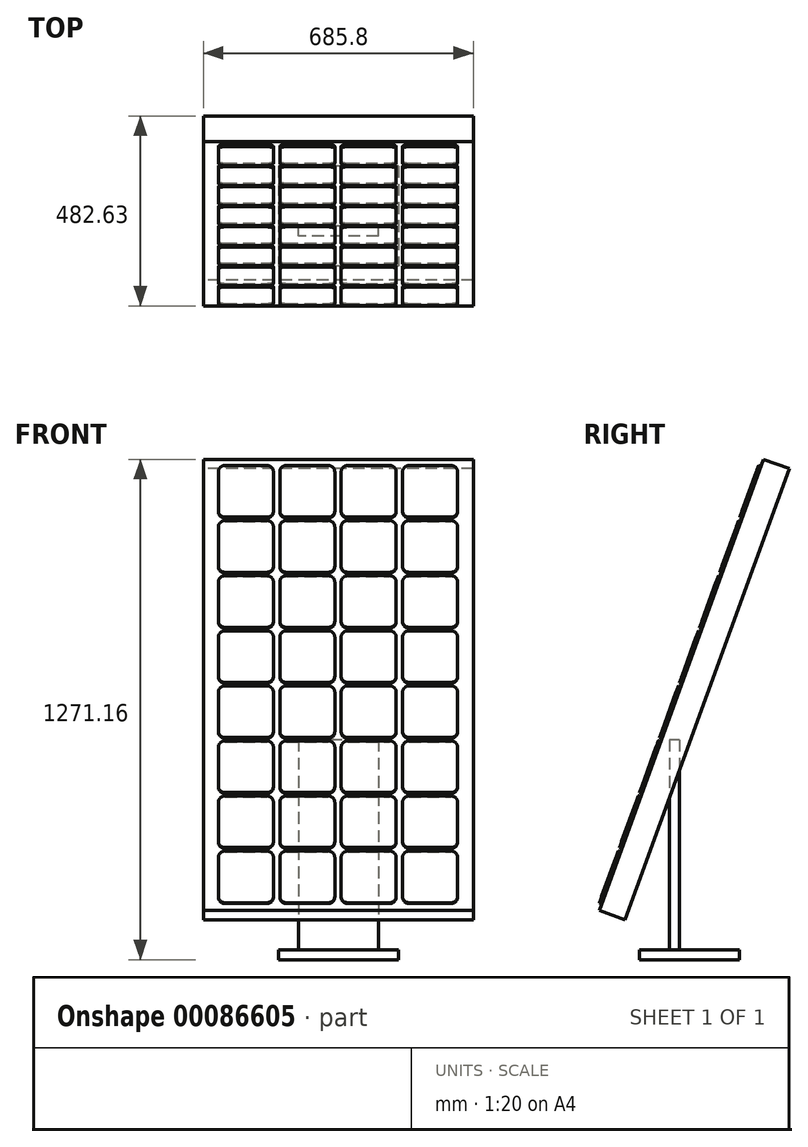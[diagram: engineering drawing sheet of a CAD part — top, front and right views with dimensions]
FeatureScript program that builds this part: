
annotation { "Feature Type Name" : "Feature", "Feature Type Description" : "" }
export const myFeature = defineFeature(function(context is Context, id is Id, definition is map)
    precondition{}
    {
        {
            var Q0;
            Q0=qCreatedBy(makeId("Right.planeOp"),FACE);
            var sketch = newSketch(context, id + "F0", { "sketchPlane" : qUnion([Q0])});
            skLineSegment(sketch, "E0", {"start": v(0, 125.5) * mm, "end": v(417, 1271.16) * mm});
            skLineSegment(sketch, "E1", {"start": v(417, 1271.16) * mm, "end": v(482.63, 1247.27) * mm});
            skLineSegment(sketch, "E2", {"start": v(482.63, 1247.27) * mm, "end": v(65.64, 101.6) * mm});
            skLineSegment(sketch, "E3", {"start": v(65.64, 101.6) * mm, "end": v(0, 125.5) * mm});
            skLineSegment(sketch, "E4", {"start": v(0, 0) * mm, "end": v(325.35, 0) * mm, "construction": true});
            skSolve(sketch);
        }
        {
            var Q0;
            Q0 = qSketchRegion(id + "F0", true);
            extrude(context, id + "F1", {"entities" : qUnion([Q0]), "depth" : 342.9 * mm, "hasSecondDirection" : true, "secondDirectionOppositeDirection" : true, "secondDirectionDepth" : 342.9 * mm});
        }
        {
            var Q0;
            Q0=qCreatedBy(makeId("Right.planeOp"),FACE);
            var sketch = newSketch(context, id + "F2", { "sketchPlane" : qUnion([Q0])});
            skLineSegment(sketch, "E5.bottom", {"start": v(203.2, 558.8) * mm, "end": v(177.8, 558.8) * mm});
            skLineSegment(sketch, "E5.top", {"start": v(203.2, 0) * mm, "end": v(177.8, 0) * mm});
            skLineSegment(sketch, "E5.left", {"start": v(203.2, 558.8) * mm, "end": v(203.2, 0) * mm});
            skLineSegment(sketch, "E5.right", {"start": v(177.8, 558.8) * mm, "end": v(177.8, 0) * mm});
            skSolve(sketch);
        }
        {
            var Q0;
            Q0 = qSketchRegion(id + "F2", true);
            extrude(context, id + "F3", {"entities" : qUnion([Q0]), "depth" : 101.6 * mm, "hasSecondDirection" : true, "secondDirectionOppositeDirection" : true, "secondDirectionDepth" : 101.6 * mm});
        }
        {
            var Q0;
            Q0=makeQuery(id+"F3.opExtrude","SWEPT_FACE",FACE,{"disambiguationData":[OSD([sQuery(id+"F2.wireOp",EDGE,"E5.top")])]});
            var sketch = newSketch(context, id + "F4", { "sketchPlane" : qUnion([Q0])});
            skLineSegment(sketch, "E6.bottom", {"start": v(152.4, -355.6) * mm, "end": v(-152.4, -355.6) * mm});
            skLineSegment(sketch, "E6.top", {"start": v(152.4, -101.6) * mm, "end": v(-152.4, -101.6) * mm});
            skLineSegment(sketch, "E6.left", {"start": v(152.4, -355.6) * mm, "end": v(152.4, -101.6) * mm});
            skLineSegment(sketch, "E6.right", {"start": v(-152.4, -355.6) * mm, "end": v(-152.4, -101.6) * mm});
            skSolve(sketch);
        }
        {
            var Q0;
            Q0 = qSketchRegion(id + "F4", true);
            extrude(context, id + "F5", {"entities" : qUnion([Q0]), "operationType" : NewBodyOperationType.ADD, "oppositeDirection" : true, "depth" : 25.4 * mm});
        }
        {
            var Q0;
            Q0=makeQuery(id+"F1.opExtrude","SWEPT_FACE",FACE,{"disambiguationData":[OSD([sQuery(id+"F0.wireOp",EDGE,"E0")])]});
            var sketch = newSketch(context, id + "F6", { "sketchPlane" : qUnion([Q0])});
            skLineSegment(sketch, "E7.bottom", {"start": v(-288.04, 1318.07) * mm, "end": v(-181.86, 1318.07) * mm});
            skLineSegment(sketch, "E7.top", {"start": v(-288.04, 1178.37) * mm, "end": v(-181.86, 1178.37) * mm});
            skLineSegment(sketch, "E7.left", {"start": v(-304.8, 1301.3) * mm, "end": v(-304.8, 1195.14) * mm});
            skLineSegment(sketch, "E7.right", {"start": v(-165.1, 1301.3) * mm, "end": v(-165.1, 1195.14) * mm});
            skPoint(sketch, "E8.visualSharp", {"position": v(-304.8, 1318.07) * mm});
            skArc(sketch, "E8.filletArc", {"start": v(-288.04, 1318.07) * mm, "mid": v(-299.89, 1313.16) * mm, "end": v(-304.8, 1301.3) * mm});
            skPoint(sketch, "E9.visualSharp", {"position": v(-165.1, 1318.07) * mm});
            skArc(sketch, "E9.filletArc", {"start": v(-165.1, 1301.3) * mm, "mid": v(-170.01, 1313.16) * mm, "end": v(-181.86, 1318.07) * mm});
            skPoint(sketch, "E10.visualSharp", {"position": v(-165.1, 1178.37) * mm});
            skArc(sketch, "E10.filletArc", {"start": v(-181.86, 1178.37) * mm, "mid": v(-170.01, 1183.28) * mm, "end": v(-165.1, 1195.14) * mm});
            skPoint(sketch, "E11.visualSharp", {"position": v(-304.8, 1178.37) * mm});
            skArc(sketch, "E11.filletArc", {"start": v(-304.8, 1195.14) * mm, "mid": v(-299.89, 1183.28) * mm, "end": v(-288.04, 1178.37) * mm});
            skLineSegment(sketch, "E12.0.1.0", {"start": v(-288.04, 1169.16) * mm, "end": v(-181.86, 1169.16) * mm});
            skLineSegment(sketch, "E12.0.1.1", {"start": v(-288.04, 1029.46) * mm, "end": v(-181.86, 1029.46) * mm});
            skLineSegment(sketch, "E12.0.1.2", {"start": v(-304.8, 1152.4) * mm, "end": v(-304.8, 1046.22) * mm});
            skLineSegment(sketch, "E12.0.1.3", {"start": v(-165.1, 1152.4) * mm, "end": v(-165.1, 1046.22) * mm});
            skPoint(sketch, "E12.0.1.4", {"position": v(-304.8, 1169.16) * mm});
            skPoint(sketch, "E12.0.1.5", {"position": v(-165.1, 1169.16) * mm});
            skPoint(sketch, "E12.0.1.6", {"position": v(-165.1, 1029.46) * mm});
            skPoint(sketch, "E12.0.1.7", {"position": v(-304.8, 1029.46) * mm});
            skArc(sketch, "E12.0.1.8", {"start": v(-288.04, 1169.16) * mm, "mid": v(-299.89, 1164.25) * mm, "end": v(-304.8, 1152.4) * mm});
            skArc(sketch, "E12.0.1.9", {"start": v(-165.1, 1152.4) * mm, "mid": v(-170.01, 1164.25) * mm, "end": v(-181.86, 1169.16) * mm});
            skArc(sketch, "E12.0.1.10", {"start": v(-181.86, 1029.46) * mm, "mid": v(-170.01, 1034.37) * mm, "end": v(-165.1, 1046.22) * mm});
            skArc(sketch, "E12.0.1.11", {"start": v(-304.8, 1046.22) * mm, "mid": v(-299.89, 1034.37) * mm, "end": v(-288.04, 1029.46) * mm});
            skLineSegment(sketch, "E12.0.2.0", {"start": v(-288.04, 1020.25) * mm, "end": v(-181.86, 1020.25) * mm});
            skLineSegment(sketch, "E12.0.2.1", {"start": v(-288.04, 880.55) * mm, "end": v(-181.86, 880.55) * mm});
            skLineSegment(sketch, "E12.0.2.2", {"start": v(-304.8, 1003.48) * mm, "end": v(-304.8, 897.31) * mm});
            skLineSegment(sketch, "E12.0.2.3", {"start": v(-165.1, 1003.48) * mm, "end": v(-165.1, 897.31) * mm});
            skPoint(sketch, "E12.0.2.4", {"position": v(-304.8, 1020.25) * mm});
            skPoint(sketch, "E12.0.2.5", {"position": v(-165.1, 1020.25) * mm});
            skPoint(sketch, "E12.0.2.6", {"position": v(-165.1, 880.55) * mm});
            skPoint(sketch, "E12.0.2.7", {"position": v(-304.8, 880.55) * mm});
            skArc(sketch, "E12.0.2.8", {"start": v(-288.04, 1020.25) * mm, "mid": v(-299.89, 1015.34) * mm, "end": v(-304.8, 1003.48) * mm});
            skArc(sketch, "E12.0.2.9", {"start": v(-165.1, 1003.48) * mm, "mid": v(-170.01, 1015.34) * mm, "end": v(-181.86, 1020.25) * mm});
            skArc(sketch, "E12.0.2.10", {"start": v(-181.86, 880.55) * mm, "mid": v(-170.01, 885.46) * mm, "end": v(-165.1, 897.31) * mm});
            skArc(sketch, "E12.0.2.11", {"start": v(-304.8, 897.31) * mm, "mid": v(-299.89, 885.46) * mm, "end": v(-288.04, 880.55) * mm});
            skLineSegment(sketch, "E12.0.3.0", {"start": v(-288.04, 871.33) * mm, "end": v(-181.86, 871.33) * mm});
            skLineSegment(sketch, "E12.0.3.1", {"start": v(-288.04, 731.63) * mm, "end": v(-181.86, 731.63) * mm});
            skLineSegment(sketch, "E12.0.3.2", {"start": v(-304.8, 854.57) * mm, "end": v(-304.8, 748.4) * mm});
            skLineSegment(sketch, "E12.0.3.3", {"start": v(-165.1, 854.57) * mm, "end": v(-165.1, 748.4) * mm});
            skPoint(sketch, "E12.0.3.4", {"position": v(-304.8, 871.33) * mm});
            skPoint(sketch, "E12.0.3.5", {"position": v(-165.1, 871.33) * mm});
            skPoint(sketch, "E12.0.3.6", {"position": v(-165.1, 731.63) * mm});
            skPoint(sketch, "E12.0.3.7", {"position": v(-304.8, 731.63) * mm});
            skArc(sketch, "E12.0.3.8", {"start": v(-288.04, 871.33) * mm, "mid": v(-299.89, 866.42) * mm, "end": v(-304.8, 854.57) * mm});
            skArc(sketch, "E12.0.3.9", {"start": v(-165.1, 854.57) * mm, "mid": v(-170.01, 866.42) * mm, "end": v(-181.86, 871.33) * mm});
            skArc(sketch, "E12.0.3.10", {"start": v(-181.86, 731.63) * mm, "mid": v(-170.01, 736.54) * mm, "end": v(-165.1, 748.4) * mm});
            skArc(sketch, "E12.0.3.11", {"start": v(-304.8, 748.4) * mm, "mid": v(-299.89, 736.54) * mm, "end": v(-288.04, 731.63) * mm});
            skLineSegment(sketch, "E12.0.4.0", {"start": v(-288.04, 722.42) * mm, "end": v(-181.86, 722.42) * mm});
            skLineSegment(sketch, "E12.0.4.1", {"start": v(-288.04, 582.72) * mm, "end": v(-181.86, 582.72) * mm});
            skLineSegment(sketch, "E12.0.4.2", {"start": v(-304.8, 705.66) * mm, "end": v(-304.8, 599.49) * mm});
            skLineSegment(sketch, "E12.0.4.3", {"start": v(-165.1, 705.66) * mm, "end": v(-165.1, 599.49) * mm});
            skPoint(sketch, "E12.0.4.4", {"position": v(-304.8, 722.42) * mm});
            skPoint(sketch, "E12.0.4.5", {"position": v(-165.1, 722.42) * mm});
            skPoint(sketch, "E12.0.4.6", {"position": v(-165.1, 582.72) * mm});
            skPoint(sketch, "E12.0.4.7", {"position": v(-304.8, 582.72) * mm});
            skArc(sketch, "E12.0.4.8", {"start": v(-288.04, 722.42) * mm, "mid": v(-299.89, 717.51) * mm, "end": v(-304.8, 705.66) * mm});
            skArc(sketch, "E12.0.4.9", {"start": v(-165.1, 705.66) * mm, "mid": v(-170.01, 717.51) * mm, "end": v(-181.86, 722.42) * mm});
            skArc(sketch, "E12.0.4.10", {"start": v(-181.86, 582.72) * mm, "mid": v(-170.01, 587.63) * mm, "end": v(-165.1, 599.49) * mm});
            skArc(sketch, "E12.0.4.11", {"start": v(-304.8, 599.49) * mm, "mid": v(-299.89, 587.63) * mm, "end": v(-288.04, 582.72) * mm});
            skLineSegment(sketch, "E12.0.5.0", {"start": v(-288.04, 573.5) * mm, "end": v(-181.86, 573.5) * mm});
            skLineSegment(sketch, "E12.0.5.1", {"start": v(-288.04, 433.8) * mm, "end": v(-181.86, 433.8) * mm});
            skLineSegment(sketch, "E12.0.5.2", {"start": v(-304.8, 556.74) * mm, "end": v(-304.8, 450.57) * mm});
            skLineSegment(sketch, "E12.0.5.3", {"start": v(-165.1, 556.74) * mm, "end": v(-165.1, 450.57) * mm});
            skPoint(sketch, "E12.0.5.4", {"position": v(-304.8, 573.5) * mm});
            skPoint(sketch, "E12.0.5.5", {"position": v(-165.1, 573.5) * mm});
            skPoint(sketch, "E12.0.5.6", {"position": v(-165.1, 433.8) * mm});
            skPoint(sketch, "E12.0.5.7", {"position": v(-304.8, 433.8) * mm});
            skArc(sketch, "E12.0.5.8", {"start": v(-288.04, 573.5) * mm, "mid": v(-299.89, 568.6) * mm, "end": v(-304.8, 556.74) * mm});
            skArc(sketch, "E12.0.5.9", {"start": v(-165.1, 556.74) * mm, "mid": v(-170.01, 568.6) * mm, "end": v(-181.86, 573.5) * mm});
            skArc(sketch, "E12.0.5.10", {"start": v(-181.86, 433.8) * mm, "mid": v(-170.01, 438.72) * mm, "end": v(-165.1, 450.57) * mm});
            skArc(sketch, "E12.0.5.11", {"start": v(-304.8, 450.57) * mm, "mid": v(-299.89, 438.72) * mm, "end": v(-288.04, 433.8) * mm});
            skLineSegment(sketch, "E12.0.6.0", {"start": v(-288.04, 424.6) * mm, "end": v(-181.86, 424.6) * mm});
            skLineSegment(sketch, "E12.0.6.1", {"start": v(-288.04, 284.9) * mm, "end": v(-181.86, 284.9) * mm});
            skLineSegment(sketch, "E12.0.6.2", {"start": v(-304.8, 407.83) * mm, "end": v(-304.8, 301.66) * mm});
            skLineSegment(sketch, "E12.0.6.3", {"start": v(-165.1, 407.83) * mm, "end": v(-165.1, 301.66) * mm});
            skPoint(sketch, "E12.0.6.4", {"position": v(-304.8, 424.6) * mm});
            skPoint(sketch, "E12.0.6.5", {"position": v(-165.1, 424.6) * mm});
            skPoint(sketch, "E12.0.6.6", {"position": v(-165.1, 284.9) * mm});
            skPoint(sketch, "E12.0.6.7", {"position": v(-304.8, 284.9) * mm});
            skArc(sketch, "E12.0.6.8", {"start": v(-288.04, 424.6) * mm, "mid": v(-299.89, 419.69) * mm, "end": v(-304.8, 407.83) * mm});
            skArc(sketch, "E12.0.6.9", {"start": v(-165.1, 407.83) * mm, "mid": v(-170.01, 419.69) * mm, "end": v(-181.86, 424.6) * mm});
            skArc(sketch, "E12.0.6.10", {"start": v(-181.86, 284.9) * mm, "mid": v(-170.01, 289.8) * mm, "end": v(-165.1, 301.66) * mm});
            skArc(sketch, "E12.0.6.11", {"start": v(-304.8, 301.66) * mm, "mid": v(-299.89, 289.8) * mm, "end": v(-288.04, 284.9) * mm});
            skLineSegment(sketch, "E12.0.7.0", {"start": v(-288.04, 275.68) * mm, "end": v(-181.86, 275.68) * mm});
            skLineSegment(sketch, "E12.0.7.1", {"start": v(-288.04, 135.98) * mm, "end": v(-181.86, 135.98) * mm});
            skLineSegment(sketch, "E12.0.7.2", {"start": v(-304.8, 258.92) * mm, "end": v(-304.8, 152.75) * mm});
            skLineSegment(sketch, "E12.0.7.3", {"start": v(-165.1, 258.92) * mm, "end": v(-165.1, 152.75) * mm});
            skPoint(sketch, "E12.0.7.4", {"position": v(-304.8, 275.68) * mm});
            skPoint(sketch, "E12.0.7.5", {"position": v(-165.1, 275.68) * mm});
            skPoint(sketch, "E12.0.7.6", {"position": v(-165.1, 135.98) * mm});
            skPoint(sketch, "E12.0.7.7", {"position": v(-304.8, 135.98) * mm});
            skArc(sketch, "E12.0.7.8", {"start": v(-288.04, 275.68) * mm, "mid": v(-299.89, 270.77) * mm, "end": v(-304.8, 258.92) * mm});
            skArc(sketch, "E12.0.7.9", {"start": v(-165.1, 258.92) * mm, "mid": v(-170.01, 270.77) * mm, "end": v(-181.86, 275.68) * mm});
            skArc(sketch, "E12.0.7.10", {"start": v(-181.86, 135.98) * mm, "mid": v(-170.01, 140.9) * mm, "end": v(-165.1, 152.75) * mm});
            skArc(sketch, "E12.0.7.11", {"start": v(-304.8, 152.75) * mm, "mid": v(-299.89, 140.9) * mm, "end": v(-288.04, 135.98) * mm});
            skLineSegment(sketch, "E12.1.0.0", {"start": v(-132.07, 1318.07) * mm, "end": v(-25.9, 1318.07) * mm});
            skLineSegment(sketch, "E12.1.0.1", {"start": v(-132.07, 1178.37) * mm, "end": v(-25.9, 1178.37) * mm});
            skLineSegment(sketch, "E12.1.0.2", {"start": v(-148.84, 1301.3) * mm, "end": v(-148.84, 1195.14) * mm});
            skLineSegment(sketch, "E12.1.0.3", {"start": v(-9.14, 1301.3) * mm, "end": v(-9.14, 1195.14) * mm});
            skPoint(sketch, "E12.1.0.4", {"position": v(-148.84, 1318.07) * mm});
            skPoint(sketch, "E12.1.0.5", {"position": v(-9.14, 1318.07) * mm});
            skPoint(sketch, "E12.1.0.6", {"position": v(-9.14, 1178.37) * mm});
            skPoint(sketch, "E12.1.0.7", {"position": v(-148.84, 1178.37) * mm});
            skArc(sketch, "E12.1.0.8", {"start": v(-132.07, 1318.07) * mm, "mid": v(-143.93, 1313.16) * mm, "end": v(-148.84, 1301.3) * mm});
            skArc(sketch, "E12.1.0.9", {"start": v(-9.14, 1301.3) * mm, "mid": v(-14.05, 1313.16) * mm, "end": v(-25.9, 1318.07) * mm});
            skArc(sketch, "E12.1.0.10", {"start": v(-25.9, 1178.37) * mm, "mid": v(-14.05, 1183.28) * mm, "end": v(-9.14, 1195.14) * mm});
            skArc(sketch, "E12.1.0.11", {"start": v(-148.84, 1195.14) * mm, "mid": v(-143.93, 1183.28) * mm, "end": v(-132.07, 1178.37) * mm});
            skLineSegment(sketch, "E12.1.1.0", {"start": v(-132.07, 1169.16) * mm, "end": v(-25.9, 1169.16) * mm});
            skLineSegment(sketch, "E12.1.1.1", {"start": v(-132.07, 1029.46) * mm, "end": v(-25.9, 1029.46) * mm});
            skLineSegment(sketch, "E12.1.1.2", {"start": v(-148.84, 1152.4) * mm, "end": v(-148.84, 1046.22) * mm});
            skLineSegment(sketch, "E12.1.1.3", {"start": v(-9.14, 1152.4) * mm, "end": v(-9.14, 1046.22) * mm});
            skPoint(sketch, "E12.1.1.4", {"position": v(-148.84, 1169.16) * mm});
            skPoint(sketch, "E12.1.1.5", {"position": v(-9.14, 1169.16) * mm});
            skPoint(sketch, "E12.1.1.6", {"position": v(-9.14, 1029.46) * mm});
            skPoint(sketch, "E12.1.1.7", {"position": v(-148.84, 1029.46) * mm});
            skArc(sketch, "E12.1.1.8", {"start": v(-132.07, 1169.16) * mm, "mid": v(-143.93, 1164.25) * mm, "end": v(-148.84, 1152.4) * mm});
            skArc(sketch, "E12.1.1.9", {"start": v(-9.14, 1152.4) * mm, "mid": v(-14.05, 1164.25) * mm, "end": v(-25.9, 1169.16) * mm});
            skArc(sketch, "E12.1.1.10", {"start": v(-25.9, 1029.46) * mm, "mid": v(-14.05, 1034.37) * mm, "end": v(-9.14, 1046.22) * mm});
            skArc(sketch, "E12.1.1.11", {"start": v(-148.84, 1046.22) * mm, "mid": v(-143.93, 1034.37) * mm, "end": v(-132.07, 1029.46) * mm});
            skLineSegment(sketch, "E12.1.2.0", {"start": v(-132.07, 1020.25) * mm, "end": v(-25.9, 1020.25) * mm});
            skLineSegment(sketch, "E12.1.2.1", {"start": v(-132.07, 880.55) * mm, "end": v(-25.9, 880.55) * mm});
            skLineSegment(sketch, "E12.1.2.2", {"start": v(-148.84, 1003.48) * mm, "end": v(-148.84, 897.31) * mm});
            skLineSegment(sketch, "E12.1.2.3", {"start": v(-9.14, 1003.48) * mm, "end": v(-9.14, 897.31) * mm});
            skPoint(sketch, "E12.1.2.4", {"position": v(-148.84, 1020.25) * mm});
            skPoint(sketch, "E12.1.2.5", {"position": v(-9.14, 1020.25) * mm});
            skPoint(sketch, "E12.1.2.6", {"position": v(-9.14, 880.55) * mm});
            skPoint(sketch, "E12.1.2.7", {"position": v(-148.84, 880.55) * mm});
            skArc(sketch, "E12.1.2.8", {"start": v(-132.07, 1020.25) * mm, "mid": v(-143.93, 1015.34) * mm, "end": v(-148.84, 1003.48) * mm});
            skArc(sketch, "E12.1.2.9", {"start": v(-9.14, 1003.48) * mm, "mid": v(-14.05, 1015.34) * mm, "end": v(-25.9, 1020.25) * mm});
            skArc(sketch, "E12.1.2.10", {"start": v(-25.9, 880.55) * mm, "mid": v(-14.05, 885.46) * mm, "end": v(-9.14, 897.31) * mm});
            skArc(sketch, "E12.1.2.11", {"start": v(-148.84, 897.31) * mm, "mid": v(-143.93, 885.46) * mm, "end": v(-132.07, 880.55) * mm});
            skLineSegment(sketch, "E12.1.3.0", {"start": v(-132.07, 871.33) * mm, "end": v(-25.9, 871.33) * mm});
            skLineSegment(sketch, "E12.1.3.1", {"start": v(-132.07, 731.63) * mm, "end": v(-25.9, 731.63) * mm});
            skLineSegment(sketch, "E12.1.3.2", {"start": v(-148.84, 854.57) * mm, "end": v(-148.84, 748.4) * mm});
            skLineSegment(sketch, "E12.1.3.3", {"start": v(-9.14, 854.57) * mm, "end": v(-9.14, 748.4) * mm});
            skPoint(sketch, "E12.1.3.4", {"position": v(-148.84, 871.33) * mm});
            skPoint(sketch, "E12.1.3.5", {"position": v(-9.14, 871.33) * mm});
            skPoint(sketch, "E12.1.3.6", {"position": v(-9.14, 731.63) * mm});
            skPoint(sketch, "E12.1.3.7", {"position": v(-148.84, 731.63) * mm});
            skArc(sketch, "E12.1.3.8", {"start": v(-132.07, 871.33) * mm, "mid": v(-143.93, 866.42) * mm, "end": v(-148.84, 854.57) * mm});
            skArc(sketch, "E12.1.3.9", {"start": v(-9.14, 854.57) * mm, "mid": v(-14.05, 866.42) * mm, "end": v(-25.9, 871.33) * mm});
            skArc(sketch, "E12.1.3.10", {"start": v(-25.9, 731.63) * mm, "mid": v(-14.05, 736.54) * mm, "end": v(-9.14, 748.4) * mm});
            skArc(sketch, "E12.1.3.11", {"start": v(-148.84, 748.4) * mm, "mid": v(-143.93, 736.54) * mm, "end": v(-132.07, 731.63) * mm});
            skLineSegment(sketch, "E12.1.4.0", {"start": v(-132.07, 722.42) * mm, "end": v(-25.9, 722.42) * mm});
            skLineSegment(sketch, "E12.1.4.1", {"start": v(-132.07, 582.72) * mm, "end": v(-25.9, 582.72) * mm});
            skLineSegment(sketch, "E12.1.4.2", {"start": v(-148.84, 705.66) * mm, "end": v(-148.84, 599.49) * mm});
            skLineSegment(sketch, "E12.1.4.3", {"start": v(-9.14, 705.66) * mm, "end": v(-9.14, 599.49) * mm});
            skPoint(sketch, "E12.1.4.4", {"position": v(-148.84, 722.42) * mm});
            skPoint(sketch, "E12.1.4.5", {"position": v(-9.14, 722.42) * mm});
            skPoint(sketch, "E12.1.4.6", {"position": v(-9.14, 582.72) * mm});
            skPoint(sketch, "E12.1.4.7", {"position": v(-148.84, 582.72) * mm});
            skArc(sketch, "E12.1.4.8", {"start": v(-132.07, 722.42) * mm, "mid": v(-143.93, 717.51) * mm, "end": v(-148.84, 705.66) * mm});
            skArc(sketch, "E12.1.4.9", {"start": v(-9.14, 705.66) * mm, "mid": v(-14.05, 717.51) * mm, "end": v(-25.9, 722.42) * mm});
            skArc(sketch, "E12.1.4.10", {"start": v(-25.9, 582.72) * mm, "mid": v(-14.05, 587.63) * mm, "end": v(-9.14, 599.49) * mm});
            skArc(sketch, "E12.1.4.11", {"start": v(-148.84, 599.49) * mm, "mid": v(-143.93, 587.63) * mm, "end": v(-132.07, 582.72) * mm});
            skLineSegment(sketch, "E12.1.5.0", {"start": v(-132.07, 573.5) * mm, "end": v(-25.9, 573.5) * mm});
            skLineSegment(sketch, "E12.1.5.1", {"start": v(-132.07, 433.8) * mm, "end": v(-25.9, 433.8) * mm});
            skLineSegment(sketch, "E12.1.5.2", {"start": v(-148.84, 556.74) * mm, "end": v(-148.84, 450.57) * mm});
            skLineSegment(sketch, "E12.1.5.3", {"start": v(-9.14, 556.74) * mm, "end": v(-9.14, 450.57) * mm});
            skPoint(sketch, "E12.1.5.4", {"position": v(-148.84, 573.5) * mm});
            skPoint(sketch, "E12.1.5.5", {"position": v(-9.14, 573.5) * mm});
            skPoint(sketch, "E12.1.5.6", {"position": v(-9.14, 433.8) * mm});
            skPoint(sketch, "E12.1.5.7", {"position": v(-148.84, 433.8) * mm});
            skArc(sketch, "E12.1.5.8", {"start": v(-132.07, 573.5) * mm, "mid": v(-143.93, 568.6) * mm, "end": v(-148.84, 556.74) * mm});
            skArc(sketch, "E12.1.5.9", {"start": v(-9.14, 556.74) * mm, "mid": v(-14.05, 568.6) * mm, "end": v(-25.9, 573.5) * mm});
            skArc(sketch, "E12.1.5.10", {"start": v(-25.9, 433.8) * mm, "mid": v(-14.05, 438.72) * mm, "end": v(-9.14, 450.57) * mm});
            skArc(sketch, "E12.1.5.11", {"start": v(-148.84, 450.57) * mm, "mid": v(-143.93, 438.72) * mm, "end": v(-132.07, 433.8) * mm});
            skLineSegment(sketch, "E12.1.6.0", {"start": v(-132.07, 424.6) * mm, "end": v(-25.9, 424.6) * mm});
            skLineSegment(sketch, "E12.1.6.1", {"start": v(-132.07, 284.9) * mm, "end": v(-25.9, 284.9) * mm});
            skLineSegment(sketch, "E12.1.6.2", {"start": v(-148.84, 407.83) * mm, "end": v(-148.84, 301.66) * mm});
            skLineSegment(sketch, "E12.1.6.3", {"start": v(-9.14, 407.83) * mm, "end": v(-9.14, 301.66) * mm});
            skPoint(sketch, "E12.1.6.4", {"position": v(-148.84, 424.6) * mm});
            skPoint(sketch, "E12.1.6.5", {"position": v(-9.14, 424.6) * mm});
            skPoint(sketch, "E12.1.6.6", {"position": v(-9.14, 284.9) * mm});
            skPoint(sketch, "E12.1.6.7", {"position": v(-148.84, 284.9) * mm});
            skArc(sketch, "E12.1.6.8", {"start": v(-132.07, 424.6) * mm, "mid": v(-143.93, 419.69) * mm, "end": v(-148.84, 407.83) * mm});
            skArc(sketch, "E12.1.6.9", {"start": v(-9.14, 407.83) * mm, "mid": v(-14.05, 419.69) * mm, "end": v(-25.9, 424.6) * mm});
            skArc(sketch, "E12.1.6.10", {"start": v(-25.9, 284.9) * mm, "mid": v(-14.05, 289.8) * mm, "end": v(-9.14, 301.66) * mm});
            skArc(sketch, "E12.1.6.11", {"start": v(-148.84, 301.66) * mm, "mid": v(-143.93, 289.8) * mm, "end": v(-132.07, 284.9) * mm});
            skLineSegment(sketch, "E12.1.7.0", {"start": v(-132.07, 275.68) * mm, "end": v(-25.9, 275.68) * mm});
            skLineSegment(sketch, "E12.1.7.1", {"start": v(-132.07, 135.98) * mm, "end": v(-25.9, 135.98) * mm});
            skLineSegment(sketch, "E12.1.7.2", {"start": v(-148.84, 258.92) * mm, "end": v(-148.84, 152.75) * mm});
            skLineSegment(sketch, "E12.1.7.3", {"start": v(-9.14, 258.92) * mm, "end": v(-9.14, 152.75) * mm});
            skPoint(sketch, "E12.1.7.4", {"position": v(-148.84, 275.68) * mm});
            skPoint(sketch, "E12.1.7.5", {"position": v(-9.14, 275.68) * mm});
            skPoint(sketch, "E12.1.7.6", {"position": v(-9.14, 135.98) * mm});
            skPoint(sketch, "E12.1.7.7", {"position": v(-148.84, 135.98) * mm});
            skArc(sketch, "E12.1.7.8", {"start": v(-132.07, 275.68) * mm, "mid": v(-143.93, 270.77) * mm, "end": v(-148.84, 258.92) * mm});
            skArc(sketch, "E12.1.7.9", {"start": v(-9.14, 258.92) * mm, "mid": v(-14.05, 270.77) * mm, "end": v(-25.9, 275.68) * mm});
            skArc(sketch, "E12.1.7.10", {"start": v(-25.9, 135.98) * mm, "mid": v(-14.05, 140.9) * mm, "end": v(-9.14, 152.75) * mm});
            skArc(sketch, "E12.1.7.11", {"start": v(-148.84, 152.75) * mm, "mid": v(-143.93, 140.9) * mm, "end": v(-132.07, 135.98) * mm});
            skLineSegment(sketch, "E12.2.0.0", {"start": v(23.89, 1318.07) * mm, "end": v(130.06, 1318.07) * mm});
            skLineSegment(sketch, "E12.2.0.1", {"start": v(23.89, 1178.37) * mm, "end": v(130.06, 1178.37) * mm});
            skLineSegment(sketch, "E12.2.0.2", {"start": v(7.13, 1301.3) * mm, "end": v(7.13, 1195.14) * mm});
            skLineSegment(sketch, "E12.2.0.3", {"start": v(146.83, 1301.3) * mm, "end": v(146.83, 1195.14) * mm});
            skPoint(sketch, "E12.2.0.4", {"position": v(7.13, 1318.07) * mm});
            skPoint(sketch, "E12.2.0.5", {"position": v(146.83, 1318.07) * mm});
            skPoint(sketch, "E12.2.0.6", {"position": v(146.83, 1178.37) * mm});
            skPoint(sketch, "E12.2.0.7", {"position": v(7.13, 1178.37) * mm});
            skArc(sketch, "E12.2.0.8", {"start": v(23.89, 1318.07) * mm, "mid": v(12.04, 1313.16) * mm, "end": v(7.13, 1301.3) * mm});
            skArc(sketch, "E12.2.0.9", {"start": v(146.83, 1301.3) * mm, "mid": v(141.92, 1313.16) * mm, "end": v(130.06, 1318.07) * mm});
            skArc(sketch, "E12.2.0.10", {"start": v(130.06, 1178.37) * mm, "mid": v(141.92, 1183.28) * mm, "end": v(146.83, 1195.14) * mm});
            skArc(sketch, "E12.2.0.11", {"start": v(7.13, 1195.14) * mm, "mid": v(12.04, 1183.28) * mm, "end": v(23.89, 1178.37) * mm});
            skLineSegment(sketch, "E12.2.1.0", {"start": v(23.89, 1169.16) * mm, "end": v(130.06, 1169.16) * mm});
            skLineSegment(sketch, "E12.2.1.1", {"start": v(23.89, 1029.46) * mm, "end": v(130.06, 1029.46) * mm});
            skLineSegment(sketch, "E12.2.1.2", {"start": v(7.13, 1152.4) * mm, "end": v(7.13, 1046.22) * mm});
            skLineSegment(sketch, "E12.2.1.3", {"start": v(146.83, 1152.4) * mm, "end": v(146.83, 1046.22) * mm});
            skPoint(sketch, "E12.2.1.4", {"position": v(7.13, 1169.16) * mm});
            skPoint(sketch, "E12.2.1.5", {"position": v(146.83, 1169.16) * mm});
            skPoint(sketch, "E12.2.1.6", {"position": v(146.83, 1029.46) * mm});
            skPoint(sketch, "E12.2.1.7", {"position": v(7.13, 1029.46) * mm});
            skArc(sketch, "E12.2.1.8", {"start": v(23.89, 1169.16) * mm, "mid": v(12.04, 1164.25) * mm, "end": v(7.13, 1152.4) * mm});
            skArc(sketch, "E12.2.1.9", {"start": v(146.83, 1152.4) * mm, "mid": v(141.92, 1164.25) * mm, "end": v(130.06, 1169.16) * mm});
            skArc(sketch, "E12.2.1.10", {"start": v(130.06, 1029.46) * mm, "mid": v(141.92, 1034.37) * mm, "end": v(146.83, 1046.22) * mm});
            skArc(sketch, "E12.2.1.11", {"start": v(7.13, 1046.22) * mm, "mid": v(12.04, 1034.37) * mm, "end": v(23.89, 1029.46) * mm});
            skLineSegment(sketch, "E12.2.2.0", {"start": v(23.89, 1020.25) * mm, "end": v(130.06, 1020.25) * mm});
            skLineSegment(sketch, "E12.2.2.1", {"start": v(23.89, 880.55) * mm, "end": v(130.06, 880.55) * mm});
            skLineSegment(sketch, "E12.2.2.2", {"start": v(7.13, 1003.48) * mm, "end": v(7.13, 897.31) * mm});
            skLineSegment(sketch, "E12.2.2.3", {"start": v(146.83, 1003.48) * mm, "end": v(146.83, 897.31) * mm});
            skPoint(sketch, "E12.2.2.4", {"position": v(7.13, 1020.25) * mm});
            skPoint(sketch, "E12.2.2.5", {"position": v(146.83, 1020.25) * mm});
            skPoint(sketch, "E12.2.2.6", {"position": v(146.83, 880.55) * mm});
            skPoint(sketch, "E12.2.2.7", {"position": v(7.13, 880.55) * mm});
            skArc(sketch, "E12.2.2.8", {"start": v(23.89, 1020.25) * mm, "mid": v(12.04, 1015.34) * mm, "end": v(7.13, 1003.48) * mm});
            skArc(sketch, "E12.2.2.9", {"start": v(146.83, 1003.48) * mm, "mid": v(141.92, 1015.34) * mm, "end": v(130.06, 1020.25) * mm});
            skArc(sketch, "E12.2.2.10", {"start": v(130.06, 880.55) * mm, "mid": v(141.92, 885.46) * mm, "end": v(146.83, 897.31) * mm});
            skArc(sketch, "E12.2.2.11", {"start": v(7.13, 897.31) * mm, "mid": v(12.04, 885.46) * mm, "end": v(23.89, 880.55) * mm});
            skLineSegment(sketch, "E12.2.3.0", {"start": v(23.89, 871.33) * mm, "end": v(130.06, 871.33) * mm});
            skLineSegment(sketch, "E12.2.3.1", {"start": v(23.89, 731.63) * mm, "end": v(130.06, 731.63) * mm});
            skLineSegment(sketch, "E12.2.3.2", {"start": v(7.13, 854.57) * mm, "end": v(7.13, 748.4) * mm});
            skLineSegment(sketch, "E12.2.3.3", {"start": v(146.83, 854.57) * mm, "end": v(146.83, 748.4) * mm});
            skPoint(sketch, "E12.2.3.4", {"position": v(7.13, 871.33) * mm});
            skPoint(sketch, "E12.2.3.5", {"position": v(146.83, 871.33) * mm});
            skPoint(sketch, "E12.2.3.6", {"position": v(146.83, 731.63) * mm});
            skPoint(sketch, "E12.2.3.7", {"position": v(7.13, 731.63) * mm});
            skArc(sketch, "E12.2.3.8", {"start": v(23.89, 871.33) * mm, "mid": v(12.04, 866.42) * mm, "end": v(7.13, 854.57) * mm});
            skArc(sketch, "E12.2.3.9", {"start": v(146.83, 854.57) * mm, "mid": v(141.92, 866.42) * mm, "end": v(130.06, 871.33) * mm});
            skArc(sketch, "E12.2.3.10", {"start": v(130.06, 731.63) * mm, "mid": v(141.92, 736.54) * mm, "end": v(146.83, 748.4) * mm});
            skArc(sketch, "E12.2.3.11", {"start": v(7.13, 748.4) * mm, "mid": v(12.04, 736.54) * mm, "end": v(23.89, 731.63) * mm});
            skLineSegment(sketch, "E12.2.4.0", {"start": v(23.89, 722.42) * mm, "end": v(130.06, 722.42) * mm});
            skLineSegment(sketch, "E12.2.4.1", {"start": v(23.89, 582.72) * mm, "end": v(130.06, 582.72) * mm});
            skLineSegment(sketch, "E12.2.4.2", {"start": v(7.13, 705.66) * mm, "end": v(7.13, 599.49) * mm});
            skLineSegment(sketch, "E12.2.4.3", {"start": v(146.83, 705.66) * mm, "end": v(146.83, 599.49) * mm});
            skPoint(sketch, "E12.2.4.4", {"position": v(7.13, 722.42) * mm});
            skPoint(sketch, "E12.2.4.5", {"position": v(146.83, 722.42) * mm});
            skPoint(sketch, "E12.2.4.6", {"position": v(146.83, 582.72) * mm});
            skPoint(sketch, "E12.2.4.7", {"position": v(7.13, 582.72) * mm});
            skArc(sketch, "E12.2.4.8", {"start": v(23.89, 722.42) * mm, "mid": v(12.04, 717.51) * mm, "end": v(7.13, 705.66) * mm});
            skArc(sketch, "E12.2.4.9", {"start": v(146.83, 705.66) * mm, "mid": v(141.92, 717.51) * mm, "end": v(130.06, 722.42) * mm});
            skArc(sketch, "E12.2.4.10", {"start": v(130.06, 582.72) * mm, "mid": v(141.92, 587.63) * mm, "end": v(146.83, 599.49) * mm});
            skArc(sketch, "E12.2.4.11", {"start": v(7.13, 599.49) * mm, "mid": v(12.04, 587.63) * mm, "end": v(23.89, 582.72) * mm});
            skLineSegment(sketch, "E12.2.5.0", {"start": v(23.89, 573.5) * mm, "end": v(130.06, 573.5) * mm});
            skLineSegment(sketch, "E12.2.5.1", {"start": v(23.89, 433.8) * mm, "end": v(130.06, 433.8) * mm});
            skLineSegment(sketch, "E12.2.5.2", {"start": v(7.13, 556.74) * mm, "end": v(7.13, 450.57) * mm});
            skLineSegment(sketch, "E12.2.5.3", {"start": v(146.83, 556.74) * mm, "end": v(146.83, 450.57) * mm});
            skPoint(sketch, "E12.2.5.4", {"position": v(7.13, 573.5) * mm});
            skPoint(sketch, "E12.2.5.5", {"position": v(146.83, 573.5) * mm});
            skPoint(sketch, "E12.2.5.6", {"position": v(146.83, 433.8) * mm});
            skPoint(sketch, "E12.2.5.7", {"position": v(7.13, 433.8) * mm});
            skArc(sketch, "E12.2.5.8", {"start": v(23.89, 573.5) * mm, "mid": v(12.04, 568.6) * mm, "end": v(7.13, 556.74) * mm});
            skArc(sketch, "E12.2.5.9", {"start": v(146.83, 556.74) * mm, "mid": v(141.92, 568.6) * mm, "end": v(130.06, 573.5) * mm});
            skArc(sketch, "E12.2.5.10", {"start": v(130.06, 433.8) * mm, "mid": v(141.92, 438.72) * mm, "end": v(146.83, 450.57) * mm});
            skArc(sketch, "E12.2.5.11", {"start": v(7.13, 450.57) * mm, "mid": v(12.04, 438.72) * mm, "end": v(23.89, 433.8) * mm});
            skLineSegment(sketch, "E12.2.6.0", {"start": v(23.89, 424.6) * mm, "end": v(130.06, 424.6) * mm});
            skLineSegment(sketch, "E12.2.6.1", {"start": v(23.89, 284.9) * mm, "end": v(130.06, 284.9) * mm});
            skLineSegment(sketch, "E12.2.6.2", {"start": v(7.13, 407.83) * mm, "end": v(7.13, 301.66) * mm});
            skLineSegment(sketch, "E12.2.6.3", {"start": v(146.83, 407.83) * mm, "end": v(146.83, 301.66) * mm});
            skPoint(sketch, "E12.2.6.4", {"position": v(7.13, 424.6) * mm});
            skPoint(sketch, "E12.2.6.5", {"position": v(146.83, 424.6) * mm});
            skPoint(sketch, "E12.2.6.6", {"position": v(146.83, 284.9) * mm});
            skPoint(sketch, "E12.2.6.7", {"position": v(7.13, 284.9) * mm});
            skArc(sketch, "E12.2.6.8", {"start": v(23.89, 424.6) * mm, "mid": v(12.04, 419.69) * mm, "end": v(7.13, 407.83) * mm});
            skArc(sketch, "E12.2.6.9", {"start": v(146.83, 407.83) * mm, "mid": v(141.92, 419.69) * mm, "end": v(130.06, 424.6) * mm});
            skArc(sketch, "E12.2.6.10", {"start": v(130.06, 284.9) * mm, "mid": v(141.92, 289.8) * mm, "end": v(146.83, 301.66) * mm});
            skArc(sketch, "E12.2.6.11", {"start": v(7.13, 301.66) * mm, "mid": v(12.04, 289.8) * mm, "end": v(23.89, 284.9) * mm});
            skLineSegment(sketch, "E12.2.7.0", {"start": v(23.89, 275.68) * mm, "end": v(130.06, 275.68) * mm});
            skLineSegment(sketch, "E12.2.7.1", {"start": v(23.89, 135.98) * mm, "end": v(130.06, 135.98) * mm});
            skLineSegment(sketch, "E12.2.7.2", {"start": v(7.13, 258.92) * mm, "end": v(7.13, 152.75) * mm});
            skLineSegment(sketch, "E12.2.7.3", {"start": v(146.83, 258.92) * mm, "end": v(146.83, 152.75) * mm});
            skPoint(sketch, "E12.2.7.4", {"position": v(7.13, 275.68) * mm});
            skPoint(sketch, "E12.2.7.5", {"position": v(146.83, 275.68) * mm});
            skPoint(sketch, "E12.2.7.6", {"position": v(146.83, 135.98) * mm});
            skPoint(sketch, "E12.2.7.7", {"position": v(7.13, 135.98) * mm});
            skArc(sketch, "E12.2.7.8", {"start": v(23.89, 275.68) * mm, "mid": v(12.04, 270.77) * mm, "end": v(7.13, 258.92) * mm});
            skArc(sketch, "E12.2.7.9", {"start": v(146.83, 258.92) * mm, "mid": v(141.92, 270.77) * mm, "end": v(130.06, 275.68) * mm});
            skArc(sketch, "E12.2.7.10", {"start": v(130.06, 135.98) * mm, "mid": v(141.92, 140.9) * mm, "end": v(146.83, 152.75) * mm});
            skArc(sketch, "E12.2.7.11", {"start": v(7.13, 152.75) * mm, "mid": v(12.04, 140.9) * mm, "end": v(23.89, 135.98) * mm});
            skLineSegment(sketch, "E12.3.0.0", {"start": v(179.85, 1318.07) * mm, "end": v(286.02, 1318.07) * mm});
            skLineSegment(sketch, "E12.3.0.1", {"start": v(179.85, 1178.37) * mm, "end": v(286.02, 1178.37) * mm});
            skLineSegment(sketch, "E12.3.0.2", {"start": v(163.09, 1301.3) * mm, "end": v(163.09, 1195.14) * mm});
            skLineSegment(sketch, "E12.3.0.3", {"start": v(302.79, 1301.3) * mm, "end": v(302.79, 1195.14) * mm});
            skPoint(sketch, "E12.3.0.4", {"position": v(163.09, 1318.07) * mm});
            skPoint(sketch, "E12.3.0.5", {"position": v(302.79, 1318.07) * mm});
            skPoint(sketch, "E12.3.0.6", {"position": v(302.79, 1178.37) * mm});
            skPoint(sketch, "E12.3.0.7", {"position": v(163.09, 1178.37) * mm});
            skArc(sketch, "E12.3.0.8", {"start": v(179.85, 1318.07) * mm, "mid": v(168, 1313.16) * mm, "end": v(163.09, 1301.3) * mm});
            skArc(sketch, "E12.3.0.9", {"start": v(302.79, 1301.3) * mm, "mid": v(297.88, 1313.16) * mm, "end": v(286.02, 1318.07) * mm});
            skArc(sketch, "E12.3.0.10", {"start": v(286.02, 1178.37) * mm, "mid": v(297.88, 1183.28) * mm, "end": v(302.79, 1195.14) * mm});
            skArc(sketch, "E12.3.0.11", {"start": v(163.09, 1195.14) * mm, "mid": v(168, 1183.28) * mm, "end": v(179.85, 1178.37) * mm});
            skLineSegment(sketch, "E12.3.1.0", {"start": v(179.85, 1169.16) * mm, "end": v(286.02, 1169.16) * mm});
            skLineSegment(sketch, "E12.3.1.1", {"start": v(179.85, 1029.46) * mm, "end": v(286.02, 1029.46) * mm});
            skLineSegment(sketch, "E12.3.1.2", {"start": v(163.09, 1152.4) * mm, "end": v(163.09, 1046.22) * mm});
            skLineSegment(sketch, "E12.3.1.3", {"start": v(302.79, 1152.4) * mm, "end": v(302.79, 1046.22) * mm});
            skPoint(sketch, "E12.3.1.4", {"position": v(163.09, 1169.16) * mm});
            skPoint(sketch, "E12.3.1.5", {"position": v(302.79, 1169.16) * mm});
            skPoint(sketch, "E12.3.1.6", {"position": v(302.79, 1029.46) * mm});
            skPoint(sketch, "E12.3.1.7", {"position": v(163.09, 1029.46) * mm});
            skArc(sketch, "E12.3.1.8", {"start": v(179.85, 1169.16) * mm, "mid": v(168, 1164.25) * mm, "end": v(163.09, 1152.4) * mm});
            skArc(sketch, "E12.3.1.9", {"start": v(302.79, 1152.4) * mm, "mid": v(297.88, 1164.25) * mm, "end": v(286.02, 1169.16) * mm});
            skArc(sketch, "E12.3.1.10", {"start": v(286.02, 1029.46) * mm, "mid": v(297.88, 1034.37) * mm, "end": v(302.79, 1046.22) * mm});
            skArc(sketch, "E12.3.1.11", {"start": v(163.09, 1046.22) * mm, "mid": v(168, 1034.37) * mm, "end": v(179.85, 1029.46) * mm});
            skLineSegment(sketch, "E12.3.2.0", {"start": v(179.85, 1020.25) * mm, "end": v(286.02, 1020.25) * mm});
            skLineSegment(sketch, "E12.3.2.1", {"start": v(179.85, 880.55) * mm, "end": v(286.02, 880.55) * mm});
            skLineSegment(sketch, "E12.3.2.2", {"start": v(163.09, 1003.48) * mm, "end": v(163.09, 897.31) * mm});
            skLineSegment(sketch, "E12.3.2.3", {"start": v(302.79, 1003.48) * mm, "end": v(302.79, 897.31) * mm});
            skPoint(sketch, "E12.3.2.4", {"position": v(163.09, 1020.25) * mm});
            skPoint(sketch, "E12.3.2.5", {"position": v(302.79, 1020.25) * mm});
            skPoint(sketch, "E12.3.2.6", {"position": v(302.79, 880.55) * mm});
            skPoint(sketch, "E12.3.2.7", {"position": v(163.09, 880.55) * mm});
            skArc(sketch, "E12.3.2.8", {"start": v(179.85, 1020.25) * mm, "mid": v(168, 1015.34) * mm, "end": v(163.09, 1003.48) * mm});
            skArc(sketch, "E12.3.2.9", {"start": v(302.79, 1003.48) * mm, "mid": v(297.88, 1015.34) * mm, "end": v(286.02, 1020.25) * mm});
            skArc(sketch, "E12.3.2.10", {"start": v(286.02, 880.55) * mm, "mid": v(297.88, 885.46) * mm, "end": v(302.79, 897.31) * mm});
            skArc(sketch, "E12.3.2.11", {"start": v(163.09, 897.31) * mm, "mid": v(168, 885.46) * mm, "end": v(179.85, 880.55) * mm});
            skLineSegment(sketch, "E12.3.3.0", {"start": v(179.85, 871.33) * mm, "end": v(286.02, 871.33) * mm});
            skLineSegment(sketch, "E12.3.3.1", {"start": v(179.85, 731.63) * mm, "end": v(286.02, 731.63) * mm});
            skLineSegment(sketch, "E12.3.3.2", {"start": v(163.09, 854.57) * mm, "end": v(163.09, 748.4) * mm});
            skLineSegment(sketch, "E12.3.3.3", {"start": v(302.79, 854.57) * mm, "end": v(302.79, 748.4) * mm});
            skPoint(sketch, "E12.3.3.4", {"position": v(163.09, 871.33) * mm});
            skPoint(sketch, "E12.3.3.5", {"position": v(302.79, 871.33) * mm});
            skPoint(sketch, "E12.3.3.6", {"position": v(302.79, 731.63) * mm});
            skPoint(sketch, "E12.3.3.7", {"position": v(163.09, 731.63) * mm});
            skArc(sketch, "E12.3.3.8", {"start": v(179.85, 871.33) * mm, "mid": v(168, 866.42) * mm, "end": v(163.09, 854.57) * mm});
            skArc(sketch, "E12.3.3.9", {"start": v(302.79, 854.57) * mm, "mid": v(297.88, 866.42) * mm, "end": v(286.02, 871.33) * mm});
            skArc(sketch, "E12.3.3.10", {"start": v(286.02, 731.63) * mm, "mid": v(297.88, 736.54) * mm, "end": v(302.79, 748.4) * mm});
            skArc(sketch, "E12.3.3.11", {"start": v(163.09, 748.4) * mm, "mid": v(168, 736.54) * mm, "end": v(179.85, 731.63) * mm});
            skLineSegment(sketch, "E12.3.4.0", {"start": v(179.85, 722.42) * mm, "end": v(286.02, 722.42) * mm});
            skLineSegment(sketch, "E12.3.4.1", {"start": v(179.85, 582.72) * mm, "end": v(286.02, 582.72) * mm});
            skLineSegment(sketch, "E12.3.4.2", {"start": v(163.09, 705.66) * mm, "end": v(163.09, 599.49) * mm});
            skLineSegment(sketch, "E12.3.4.3", {"start": v(302.79, 705.66) * mm, "end": v(302.79, 599.49) * mm});
            skPoint(sketch, "E12.3.4.4", {"position": v(163.09, 722.42) * mm});
            skPoint(sketch, "E12.3.4.5", {"position": v(302.79, 722.42) * mm});
            skPoint(sketch, "E12.3.4.6", {"position": v(302.79, 582.72) * mm});
            skPoint(sketch, "E12.3.4.7", {"position": v(163.09, 582.72) * mm});
            skArc(sketch, "E12.3.4.8", {"start": v(179.85, 722.42) * mm, "mid": v(168, 717.51) * mm, "end": v(163.09, 705.66) * mm});
            skArc(sketch, "E12.3.4.9", {"start": v(302.79, 705.66) * mm, "mid": v(297.88, 717.51) * mm, "end": v(286.02, 722.42) * mm});
            skArc(sketch, "E12.3.4.10", {"start": v(286.02, 582.72) * mm, "mid": v(297.88, 587.63) * mm, "end": v(302.79, 599.49) * mm});
            skArc(sketch, "E12.3.4.11", {"start": v(163.09, 599.49) * mm, "mid": v(168, 587.63) * mm, "end": v(179.85, 582.72) * mm});
            skLineSegment(sketch, "E12.3.5.0", {"start": v(179.85, 573.5) * mm, "end": v(286.02, 573.5) * mm});
            skLineSegment(sketch, "E12.3.5.1", {"start": v(179.85, 433.8) * mm, "end": v(286.02, 433.8) * mm});
            skLineSegment(sketch, "E12.3.5.2", {"start": v(163.09, 556.74) * mm, "end": v(163.09, 450.57) * mm});
            skLineSegment(sketch, "E12.3.5.3", {"start": v(302.79, 556.74) * mm, "end": v(302.79, 450.57) * mm});
            skPoint(sketch, "E12.3.5.4", {"position": v(163.09, 573.5) * mm});
            skPoint(sketch, "E12.3.5.5", {"position": v(302.79, 573.5) * mm});
            skPoint(sketch, "E12.3.5.6", {"position": v(302.79, 433.8) * mm});
            skPoint(sketch, "E12.3.5.7", {"position": v(163.09, 433.8) * mm});
            skArc(sketch, "E12.3.5.8", {"start": v(179.85, 573.5) * mm, "mid": v(168, 568.6) * mm, "end": v(163.09, 556.74) * mm});
            skArc(sketch, "E12.3.5.9", {"start": v(302.79, 556.74) * mm, "mid": v(297.88, 568.6) * mm, "end": v(286.02, 573.5) * mm});
            skArc(sketch, "E12.3.5.10", {"start": v(286.02, 433.8) * mm, "mid": v(297.88, 438.72) * mm, "end": v(302.79, 450.57) * mm});
            skArc(sketch, "E12.3.5.11", {"start": v(163.09, 450.57) * mm, "mid": v(168, 438.72) * mm, "end": v(179.85, 433.8) * mm});
            skLineSegment(sketch, "E12.3.6.0", {"start": v(179.85, 424.6) * mm, "end": v(286.02, 424.6) * mm});
            skLineSegment(sketch, "E12.3.6.1", {"start": v(179.85, 284.9) * mm, "end": v(286.02, 284.9) * mm});
            skLineSegment(sketch, "E12.3.6.2", {"start": v(163.09, 407.83) * mm, "end": v(163.09, 301.66) * mm});
            skLineSegment(sketch, "E12.3.6.3", {"start": v(302.79, 407.83) * mm, "end": v(302.79, 301.66) * mm});
            skPoint(sketch, "E12.3.6.4", {"position": v(163.09, 424.6) * mm});
            skPoint(sketch, "E12.3.6.5", {"position": v(302.79, 424.6) * mm});
            skPoint(sketch, "E12.3.6.6", {"position": v(302.79, 284.9) * mm});
            skPoint(sketch, "E12.3.6.7", {"position": v(163.09, 284.9) * mm});
            skArc(sketch, "E12.3.6.8", {"start": v(179.85, 424.6) * mm, "mid": v(168, 419.69) * mm, "end": v(163.09, 407.83) * mm});
            skArc(sketch, "E12.3.6.9", {"start": v(302.79, 407.83) * mm, "mid": v(297.88, 419.69) * mm, "end": v(286.02, 424.6) * mm});
            skArc(sketch, "E12.3.6.10", {"start": v(286.02, 284.9) * mm, "mid": v(297.88, 289.8) * mm, "end": v(302.79, 301.66) * mm});
            skArc(sketch, "E12.3.6.11", {"start": v(163.09, 301.66) * mm, "mid": v(168, 289.8) * mm, "end": v(179.85, 284.9) * mm});
            skLineSegment(sketch, "E12.3.7.0", {"start": v(179.85, 275.68) * mm, "end": v(286.02, 275.68) * mm});
            skLineSegment(sketch, "E12.3.7.1", {"start": v(179.85, 135.98) * mm, "end": v(286.02, 135.98) * mm});
            skLineSegment(sketch, "E12.3.7.2", {"start": v(163.09, 258.92) * mm, "end": v(163.09, 152.75) * mm});
            skLineSegment(sketch, "E12.3.7.3", {"start": v(302.79, 258.92) * mm, "end": v(302.79, 152.75) * mm});
            skPoint(sketch, "E12.3.7.4", {"position": v(163.09, 275.68) * mm});
            skPoint(sketch, "E12.3.7.5", {"position": v(302.79, 275.68) * mm});
            skPoint(sketch, "E12.3.7.6", {"position": v(302.79, 135.98) * mm});
            skPoint(sketch, "E12.3.7.7", {"position": v(163.09, 135.98) * mm});
            skArc(sketch, "E12.3.7.8", {"start": v(179.85, 275.68) * mm, "mid": v(168, 270.77) * mm, "end": v(163.09, 258.92) * mm});
            skArc(sketch, "E12.3.7.9", {"start": v(302.79, 258.92) * mm, "mid": v(297.88, 270.77) * mm, "end": v(286.02, 275.68) * mm});
            skArc(sketch, "E12.3.7.10", {"start": v(286.02, 135.98) * mm, "mid": v(297.88, 140.9) * mm, "end": v(302.79, 152.75) * mm});
            skArc(sketch, "E12.3.7.11", {"start": v(163.09, 152.75) * mm, "mid": v(168, 140.9) * mm, "end": v(179.85, 135.98) * mm});
            skLineSegment(sketch, "E12.direction1", {"start": v(-288.04, 1318.07) * mm, "end": v(-132.07, 1318.07) * mm, "construction": true});
            skLineSegment(sketch, "E12.direction2", {"start": v(-288.04, 1318.07) * mm, "end": v(-288.04, 1169.16) * mm, "construction": true});
            skSolve(sketch);
        }
        {
            var Q0;
            Q0 = qSketchRegion(id + "F6", true);
            extrude(context, id + "F7", {"entities" : qUnion([Q0]), "depth" : 6.35 * mm});
        }
    });
